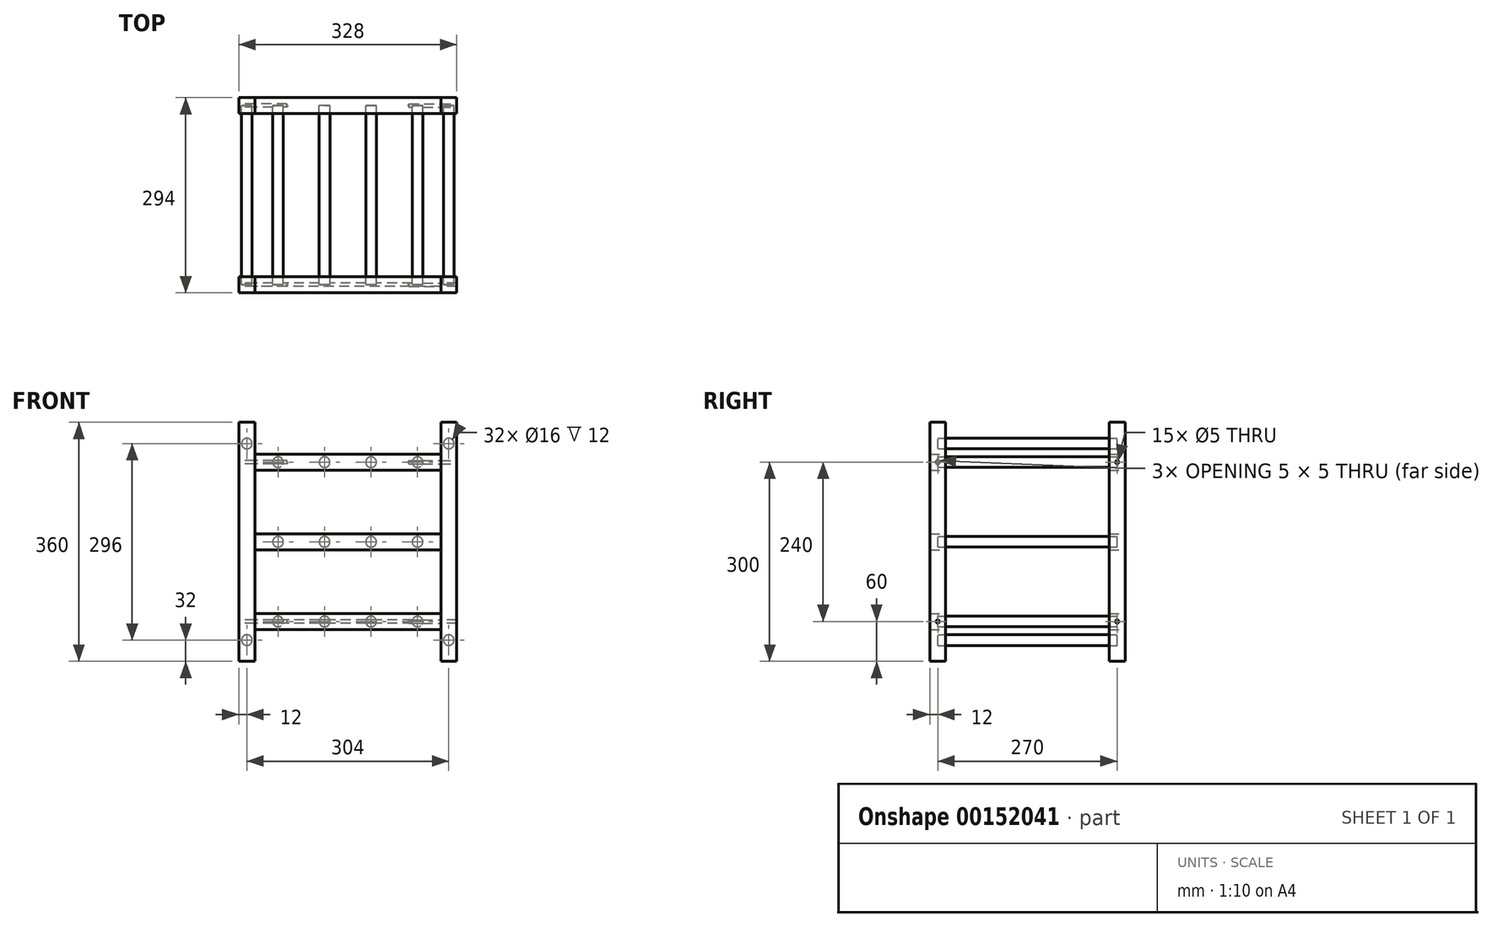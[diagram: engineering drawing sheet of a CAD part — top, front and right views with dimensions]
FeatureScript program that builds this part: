
annotation { "Feature Type Name" : "Feature", "Feature Type Description" : "" }
export const myFeature = defineFeature(function(context is Context, id is Id, definition is map)
    precondition{}
    {
        {
            assignVariable(context, id + "F0", {"name" : "Length1", "anyValue" : 270});
        }
        {
            assignVariable(context, id + "F1", {"name" : "Dia1", "anyValue" : 16 * mm});
        }
        {
            assignVariable(context, id + "F2", {"name" : "Dist1", "anyValue" : 70 * mm});
        }
        {
            assignVariable(context, id + "F3", {"name" : "Dwars1", "anyValue" : 1.5 * (getVariable(context, 'Dia1'))});
        }
        {
            assignVariable(context, id + "F4", {"name" : "Height1", "anyValue" : 120 * mm});
        }
        {
            var Q0;
            Q0=qCreatedBy(makeId("Front.planeOp"),FACE);
            var sketch = newSketch(context, id + "F5", { "sketchPlane" : qUnion([Q0])});
            skCircle(sketch, "E0", {"center": v(-105, 0) * mm, "radius": 8 * mm});
            skCircle(sketch, "E1", {"center": v(-35, 0) * mm, "radius": 8 * mm});
            skCircle(sketch, "E2", {"center": v(35, 0) * mm, "radius": 8 * mm});
            skCircle(sketch, "E3", {"center": v(105, 0) * mm, "radius": 8 * mm});
            skSolve(sketch);
        }
        {
            var Q0;
            Q0 = qSketchRegion(id + "F5", true);
            extrude(context, id + "F6", {"entities" : qUnion([Q0]), "depth" : (getVariable(context, 'Length1')) * mm});
        }
        {
            var Q0;
            Q0=qCreatedBy(makeId("Right.planeOp"),FACE);
            var sketch = newSketch(context, id + "F7", { "sketchPlane" : qUnion([Q0])});
            skLineSegment(sketch, "E4.bottom", {"start": v(-12, 12) * mm, "end": v(12, 12) * mm});
            skLineSegment(sketch, "E4.top", {"start": v(-12, -12) * mm, "end": v(12, -12) * mm});
            skLineSegment(sketch, "E4.left", {"start": v(-12, 12) * mm, "end": v(-12, -12) * mm});
            skLineSegment(sketch, "E4.right", {"start": v(12, 12) * mm, "end": v(12, -12) * mm});
            skPoint(sketch, "E5", {"position": v(12, 0) * mm});
            skPoint(sketch, "E6", {"position": v(0, 12) * mm});
            skLineSegment(sketch, "E7.bottom", {"start": v(-282, 12) * mm, "end": v(-258, 12) * mm});
            skLineSegment(sketch, "E7.top", {"start": v(-282, -12) * mm, "end": v(-258, -12) * mm});
            skLineSegment(sketch, "E7.left", {"start": v(-282, 12) * mm, "end": v(-282, -12) * mm});
            skLineSegment(sketch, "E7.right", {"start": v(-258, 12) * mm, "end": v(-258, -12) * mm});
            skPoint(sketch, "E8", {"position": v(-258, 0) * mm});
            skPoint(sketch, "E9", {"position": v(-270, 12) * mm});
            skSolve(sketch);
        }
        {
            var Q0;
            Q0 = qSketchRegion(id + "F7", true);
            extrude(context, id + "F8", {"entities" : qUnion([Q0]), "endBound" : BoundingType.SYMMETRIC, "depth" : 4 * (getVariable(context, 'Dist1'))});
        }
        {
            var Q0;
            Q0=makeQuery(id+"F6.opExtrude","SWEPT_BODY",BODY,{"disambiguationData":[OSD([sQuery(id+"F5.wireOp",EDGE,"E3")])]});
            transform(context, id + "F9", {"entities" : qUnion([Q0]), "transformType" : TransformType.COPY});
        }
        {
            var Q0;
            Q0=makeQuery(id+"F6.opExtrude","SWEPT_BODY",BODY,{"disambiguationData":[OSD([sQuery(id+"F5.wireOp",EDGE,"E0")])]});
            var Q1;
            Q1=makeQuery(id+"F6.opExtrude","SWEPT_BODY",BODY,{"disambiguationData":[OSD([sQuery(id+"F5.wireOp",EDGE,"E1")])]});
            var Q2;
            Q2=makeQuery(id+"F6.opExtrude","SWEPT_BODY",BODY,{"disambiguationData":[OSD([sQuery(id+"F5.wireOp",EDGE,"E2")])]});
            var Q3;
            Q3=makeQuery(id+"F9.opPattern","COPY",BODY,{"derivedFrom":makeQuery(id+"F6.opExtrude","SWEPT_BODY",BODY,{"disambiguationData":[OSD([sQuery(id+"F5.wireOp",EDGE,"E3")])]}),"instanceName":"1"});
            var Q4;
            Q4=makeQuery(id+"F8.opExtrude","SWEPT_BODY",BODY,{"disambiguationData":[OSD([sQuery(id+"F7.wireOp",EDGE,"E4.bottom"),sQuery(id+"F7.wireOp",EDGE,"E4.top"),sQuery(id+"F7.wireOp",EDGE,"E4.left"),sQuery(id+"F7.wireOp",EDGE,"E4.right")])]});
            var Q5;
            Q5=makeQuery(id+"F8.opExtrude","SWEPT_BODY",BODY,{"disambiguationData":[OSD([sQuery(id+"F7.wireOp",EDGE,"E7.bottom"),sQuery(id+"F7.wireOp",EDGE,"E7.top"),sQuery(id+"F7.wireOp",EDGE,"E7.left"),sQuery(id+"F7.wireOp",EDGE,"E7.right")])]});
            booleanBodies(context, id + "F10", {"operationType" : BooleanOperationType.SUBTRACTION, "tools" : qUnion([Q0, Q1, Q2, Q3]), "targets" : qUnion([Q4, Q5])});
        }
        {
            var Q0;
            Q0=makeQuery(id+"F6.opExtrude","SWEPT_BODY",BODY,{"disambiguationData":[OSD([sQuery(id+"F5.wireOp",EDGE,"E3")])]});
            transform(context, id + "F11", {"entities" : qUnion([Q0]), "transformType" : TransformType.TRANSLATION_3D, "dx" : -getVariable(context, 'Dist1'), "dy" : 0 * mm, "dz" : 0 * mm, "makeCopy" : true});
        }
        {
            var Q0;
            Q0=makeQuery(id+"F11.opPattern","COPY",BODY,{"derivedFrom":makeQuery(id+"F6.opExtrude","SWEPT_BODY",BODY,{"disambiguationData":[OSD([sQuery(id+"F5.wireOp",EDGE,"E3")])]}),"instanceName":"1"});
            var Q1;
            Q1=makeQuery(id+"F6.opExtrude","SWEPT_BODY",BODY,{"disambiguationData":[OSD([sQuery(id+"F5.wireOp",EDGE,"E3")])]});
            transform(context, id + "F12", {"entities" : qUnion([Q0, Q1]), "transformType" : TransformType.TRANSLATION_3D, "dx" : -getVariable(context, 'Dist1') * 2, "dy" : 0 * mm, "dz" : 0 * mm, "makeCopy" : true});
        }
        {
            var Q0;
            Q0=makeQuery(id+"F6.opExtrude","SWEPT_BODY",BODY,{"disambiguationData":[OSD([sQuery(id+"F5.wireOp",EDGE,"E3")])]});
            var Q1;
            Q1=makeQuery(id+"F8.opExtrude","SWEPT_BODY",BODY,{"disambiguationData":[OSD([sQuery(id+"F7.wireOp",EDGE,"E4.bottom"),sQuery(id+"F7.wireOp",EDGE,"E4.top"),sQuery(id+"F7.wireOp",EDGE,"E4.left"),sQuery(id+"F7.wireOp",EDGE,"E4.right")])]});
            var Q2;
            Q2=makeQuery(id+"F8.opExtrude","SWEPT_BODY",BODY,{"disambiguationData":[OSD([sQuery(id+"F7.wireOp",EDGE,"E7.bottom"),sQuery(id+"F7.wireOp",EDGE,"E7.top"),sQuery(id+"F7.wireOp",EDGE,"E7.left"),sQuery(id+"F7.wireOp",EDGE,"E7.right")])]});
            var Q3;
            Q3=makeQuery(id+"F11.opPattern","COPY",BODY,{"derivedFrom":makeQuery(id+"F6.opExtrude","SWEPT_BODY",BODY,{"disambiguationData":[OSD([sQuery(id+"F5.wireOp",EDGE,"E3")])]}),"instanceName":"1"});
            var Q4;
            Q4=makeQuery(id+"F12.opPattern","COPY",BODY,{"derivedFrom":makeQuery(id+"F6.opExtrude","SWEPT_BODY",BODY,{"disambiguationData":[OSD([sQuery(id+"F5.wireOp",EDGE,"E3")])]}),"instanceName":"1"});
            var Q5;
            Q5=makeQuery(id+"F12.opPattern","COPY",BODY,{"derivedFrom":makeQuery(id+"F11.opPattern","COPY",BODY,{"derivedFrom":makeQuery(id+"F6.opExtrude","SWEPT_BODY",BODY,{"disambiguationData":[OSD([sQuery(id+"F5.wireOp",EDGE,"E3")])]}),"instanceName":"1"}),"instanceName":"1"});
            transform(context, id + "F13", {"entities" : qUnion([Q0, Q1, Q2, Q3, Q4, Q5]), "transformType" : TransformType.TRANSLATION_3D, "dx" : 0 * mm, "dy" : 0 * mm, "dz" : getVariable(context, 'Height1'), "makeCopy" : true});
        }
        {
            var Q0;
            Q0=makeQuery(id+"F13.opPattern","COPY",BODY,{"derivedFrom":makeQuery(id+"F8.opExtrude","SWEPT_BODY",BODY,{"disambiguationData":[OSD([sQuery(id+"F7.wireOp",EDGE,"E7.bottom"),sQuery(id+"F7.wireOp",EDGE,"E7.top"),sQuery(id+"F7.wireOp",EDGE,"E7.left"),sQuery(id+"F7.wireOp",EDGE,"E7.right")])]}),"instanceName":"1"});
            var Q1;
            Q1=makeQuery(id+"F13.opPattern","COPY",BODY,{"derivedFrom":makeQuery(id+"F8.opExtrude","SWEPT_BODY",BODY,{"disambiguationData":[OSD([sQuery(id+"F7.wireOp",EDGE,"E4.bottom"),sQuery(id+"F7.wireOp",EDGE,"E4.top"),sQuery(id+"F7.wireOp",EDGE,"E4.left"),sQuery(id+"F7.wireOp",EDGE,"E4.right")])]}),"instanceName":"1"});
            var Q2;
            Q2=makeQuery(id+"F13.opPattern","COPY",BODY,{"derivedFrom":makeQuery(id+"F6.opExtrude","SWEPT_BODY",BODY,{"disambiguationData":[OSD([sQuery(id+"F5.wireOp",EDGE,"E3")])]}),"instanceName":"1"});
            var Q3;
            Q3=makeQuery(id+"F13.opPattern","COPY",BODY,{"derivedFrom":makeQuery(id+"F11.opPattern","COPY",BODY,{"derivedFrom":makeQuery(id+"F6.opExtrude","SWEPT_BODY",BODY,{"disambiguationData":[OSD([sQuery(id+"F5.wireOp",EDGE,"E3")])]}),"instanceName":"1"}),"instanceName":"1"});
            var Q4;
            Q4=makeQuery(id+"F13.opPattern","COPY",BODY,{"derivedFrom":makeQuery(id+"F12.opPattern","COPY",BODY,{"derivedFrom":makeQuery(id+"F6.opExtrude","SWEPT_BODY",BODY,{"disambiguationData":[OSD([sQuery(id+"F5.wireOp",EDGE,"E3")])]}),"instanceName":"1"}),"instanceName":"1"});
            var Q5;
            Q5=makeQuery(id+"F13.opPattern","COPY",BODY,{"derivedFrom":makeQuery(id+"F12.opPattern","COPY",BODY,{"derivedFrom":makeQuery(id+"F11.opPattern","COPY",BODY,{"derivedFrom":makeQuery(id+"F6.opExtrude","SWEPT_BODY",BODY,{"disambiguationData":[OSD([sQuery(id+"F5.wireOp",EDGE,"E3")])]}),"instanceName":"1"}),"instanceName":"1"}),"instanceName":"1"});
            transform(context, id + "F14", {"entities" : qUnion([Q0, Q1, Q2, Q3, Q4, Q5]), "transformType" : TransformType.TRANSLATION_3D, "dx" : 0 * mm, "dy" : 0 * mm, "dz" : getVariable(context, 'Height1'), "makeCopy" : true});
        }
        {
            var Q0;
            Q0=makeQuery(id+"F14.opPattern","COPY",FACE,{"derivedFrom":makeQuery(id+"F13.opPattern","COPY",FACE,{"derivedFrom":makeQuery(id+"F8.opExtrude","SWEPT_FACE",FACE,{"disambiguationData":[OSD([sQuery(id+"F7.wireOp",EDGE,"E7.bottom")])]}),"instanceName":"1"}),"instanceName":"1"});
            cPlane(context, id + "F15", {"entities" : qUnion([Q0]), "cplaneType" : CPlaneType.OFFSET, "offset" : getVariable(context, 'Height1') / 2 + getVariable(context, 'Dwars1') / 2, "width" : 150 * mm, "height" : 150 * mm});
        }
        {
            var Q0;
            Q0=makeQuery(id+"F14.opPattern","COPY",FACE,{"derivedFrom":makeQuery(id+"F13.opPattern","COPY",FACE,{"derivedFrom":makeQuery(id+"F8.opExtrude","CAP_FACE",FACE,{"disambiguationData":[OSD([sQuery(id+"F7.wireOp",EDGE,"E7.bottom"),sQuery(id+"F7.wireOp",EDGE,"E7.top"),sQuery(id+"F7.wireOp",EDGE,"E7.left"),sQuery(id+"F7.wireOp",EDGE,"E7.right")])],"isStart":false}),"instanceName":"1"}),"instanceName":"1"});
            cPlane(context, id + "F16", {"entities" : qUnion([Q0]), "cplaneType" : CPlaneType.OFFSET, "offset" : 0 * mm, "width" : 150 * mm, "height" : 150 * mm});
        }
        {
            var Q0;
            Q0=qCreatedBy(id+"F16.planeOp",FACE);
            var sketch = newSketch(context, id + "F17", { "sketchPlane" : qUnion([Q0])});
            skLineSegment(sketch, "E10.bottom", {"start": v(-282, 300) * mm, "end": v(-258, 300) * mm});
            skLineSegment(sketch, "E10.top", {"start": v(-282, -60) * mm, "end": v(-258, -60) * mm});
            skLineSegment(sketch, "E10.left", {"start": v(-282, 300) * mm, "end": v(-282, -60) * mm});
            skLineSegment(sketch, "E10.right", {"start": v(-258, 300) * mm, "end": v(-258, -60) * mm});
            skLineSegment(sketch, "E11", {"start": v(-282, 252) * mm, "end": v(-282, 228) * mm, "construction": true});
            skPoint(sketch, "E12", {"position": v(-282, 240) * mm});
            skLineSegment(sketch, "E13", {"start": v(-282, 12) * mm, "end": v(-282, -12) * mm, "construction": true});
            skPoint(sketch, "E14", {"position": v(-282, 0) * mm});
            skPoint(sketch, "E15", {"position": v(-282, 12) * mm});
            skPoint(sketch, "E16", {"position": v(-258, 228) * mm});
            skLineSegment(sketch, "E17", {"start": v(-258, 228) * mm, "end": v(-12, 228) * mm, "construction": true});
            skPoint(sketch, "E18", {"position": v(-135, 228) * mm});
            skLineSegment(sketch, "E19", {"start": v(-135, 228) * mm, "end": v(-135, 147.73) * mm, "construction": true});
            skLineSegment(sketch, "E20.MirrorCS", {"start": v(12, -60) * mm, "end": v(-12, -60) * mm});
            skLineSegment(sketch, "E21.MirrorCS", {"start": v(12, 300) * mm, "end": v(-12, 300) * mm});
            skLineSegment(sketch, "E22.MirrorCS", {"start": v(12, 12) * mm, "end": v(12, -12) * mm, "construction": true});
            skLineSegment(sketch, "E23.MirrorCS", {"start": v(12, 252) * mm, "end": v(12, 228) * mm, "construction": true});
            skLineSegment(sketch, "E24.MirrorCS", {"start": v(-12, 300) * mm, "end": v(-12, -60) * mm});
            skLineSegment(sketch, "E25.MirrorCS", {"start": v(12, 300) * mm, "end": v(12, -60) * mm});
            skPoint(sketch, "E26.MirrorP", {"position": v(12, 0) * mm});
            skPoint(sketch, "E27.MirrorP", {"position": v(12, 240) * mm});
            skPoint(sketch, "E28.MirrorP", {"position": v(12, 12) * mm});
            skPoint(sketch, "E29.MirrorP", {"position": v(-12, 228) * mm});
            skSolve(sketch);
        }
        {
            var Q0;
            Q0 = qSketchRegion(id + "F17", true);
            extrude(context, id + "F18", {"entities" : qUnion([Q0]), "depth" : getVariable(context, 'Dwars1')});
        }
        {
            var Q0;
            Q0=makeQuery(id+"F18.opExtrude","SWEPT_BODY",BODY,{"disambiguationData":[OSD([sQuery(id+"F17.wireOp",EDGE,"E20.MirrorCS"),sQuery(id+"F17.wireOp",EDGE,"E21.MirrorCS"),sQuery(id+"F17.wireOp",EDGE,"E24.MirrorCS"),sQuery(id+"F17.wireOp",EDGE,"E25.MirrorCS")])]});
            var Q1;
            Q1=makeQuery(id+"F18.opExtrude","SWEPT_BODY",BODY,{"disambiguationData":[OSD([sQuery(id+"F17.wireOp",EDGE,"E10.bottom"),sQuery(id+"F17.wireOp",EDGE,"E10.top"),sQuery(id+"F17.wireOp",EDGE,"E10.left"),sQuery(id+"F17.wireOp",EDGE,"E10.right")])]});
            transform(context, id + "F19", {"entities" : qUnion([Q0, Q1]), "transformType" : TransformType.TRANSLATION_3D, "dx" : -4 * getVariable(context, 'Dist1') - getVariable(context, 'Dwars1'), "dy" : 0 * mm, "dz" : 0 * mm, "makeCopy" : true});
        }
        {
            var Q0;
            Q0=makeQuery(id+"F18.opExtrude","SWEPT_FACE",FACE,{"disambiguationData":[OSD([sQuery(id+"F17.wireOp",EDGE,"E24.MirrorCS")])]});
            cPlane(context, id + "F20", {"entities" : qUnion([Q0]), "cplaneType" : CPlaneType.OFFSET, "offset" : getVariable(context, 'Dwars1') / 2, "oppositeDirection" : true, "width" : 150 * mm, "height" : 150 * mm});
        }
        {
            var Q0;
            Q0=qCreatedBy(id+"F20.planeOp",FACE);
            var sketch = newSketch(context, id + "F21", { "sketchPlane" : qUnion([Q0])});
            skCircle(sketch, "E30", {"center": v(152, 268) * mm, "radius": 8 * mm});
            skLineSegment(sketch, "E31", {"start": v(164, 268) * mm, "end": v(140, 268) * mm, "construction": true});
            skLineSegment(sketch, "E32", {"start": v(140, 300) * mm, "end": v(-140, 300) * mm, "construction": true});
            skLineSegment(sketch, "E33", {"start": v(0, 300) * mm, "end": v(0, -60) * mm, "construction": true});
            skLineSegment(sketch, "E34", {"start": v(0, 120) * mm, "end": v(-243.93, 120) * mm, "construction": true});
            skPoint(sketch, "E34.endSnap0", {"position": v(0, 120) * mm});
            skCircle(sketch, "E35.MirrorC", {"center": v(152, -28) * mm, "radius": 8 * mm});
            skCircle(sketch, "E36.MirrorC", {"center": v(-152, -28) * mm, "radius": 8 * mm});
            skCircle(sketch, "E37.MirrorC", {"center": v(-152, 268) * mm, "radius": 8 * mm});
            skSolve(sketch);
        }
        {
            var Q0;
            Q0 = qSketchRegion(id + "F21", true);
            extrude(context, id + "F22", {"entities" : qUnion([Q0]), "depth" : getVariable(context, 'Length1') * mm});
        }
        {
            var Q0;
            Q0=makeQuery(id+"F22.opExtrude","SWEPT_BODY",BODY,{"disambiguationData":[OSD([sQuery(id+"F21.wireOp",EDGE,"E30")])]});
            var Q1;
            Q1=makeQuery(id+"F22.opExtrude","SWEPT_BODY",BODY,{"disambiguationData":[OSD([sQuery(id+"F21.wireOp",EDGE,"E35.MirrorC")])]});
            var Q2;
            Q2=makeQuery(id+"F22.opExtrude","SWEPT_BODY",BODY,{"disambiguationData":[OSD([sQuery(id+"F21.wireOp",EDGE,"E36.MirrorC")])]});
            var Q3;
            Q3=makeQuery(id+"F22.opExtrude","SWEPT_BODY",BODY,{"disambiguationData":[OSD([sQuery(id+"F21.wireOp",EDGE,"E37.MirrorC")])]});
            var Q4;
            Q4=makeQuery(id+"F19.opPattern","COPY",BODY,{"derivedFrom":makeQuery(id+"F18.opExtrude","SWEPT_BODY",BODY,{"disambiguationData":[OSD([sQuery(id+"F17.wireOp",EDGE,"E10.bottom"),sQuery(id+"F17.wireOp",EDGE,"E10.top"),sQuery(id+"F17.wireOp",EDGE,"E10.left"),sQuery(id+"F17.wireOp",EDGE,"E10.right")])]}),"instanceName":"1"});
            var Q5;
            Q5=makeQuery(id+"F19.opPattern","COPY",BODY,{"derivedFrom":makeQuery(id+"F18.opExtrude","SWEPT_BODY",BODY,{"disambiguationData":[OSD([sQuery(id+"F17.wireOp",EDGE,"E20.MirrorCS"),sQuery(id+"F17.wireOp",EDGE,"E21.MirrorCS"),sQuery(id+"F17.wireOp",EDGE,"E24.MirrorCS"),sQuery(id+"F17.wireOp",EDGE,"E25.MirrorCS")])]}),"instanceName":"1"});
            var Q6;
            Q6=makeQuery(id+"F18.opExtrude","SWEPT_BODY",BODY,{"disambiguationData":[OSD([sQuery(id+"F17.wireOp",EDGE,"E20.MirrorCS"),sQuery(id+"F17.wireOp",EDGE,"E21.MirrorCS"),sQuery(id+"F17.wireOp",EDGE,"E24.MirrorCS"),sQuery(id+"F17.wireOp",EDGE,"E25.MirrorCS")])]});
            var Q7;
            Q7=makeQuery(id+"F18.opExtrude","SWEPT_BODY",BODY,{"disambiguationData":[OSD([sQuery(id+"F17.wireOp",EDGE,"E10.bottom"),sQuery(id+"F17.wireOp",EDGE,"E10.top"),sQuery(id+"F17.wireOp",EDGE,"E10.left"),sQuery(id+"F17.wireOp",EDGE,"E10.right")])]});
            booleanBodies(context, id + "F23", {"operationType" : BooleanOperationType.SUBTRACTION, "tools" : qUnion([Q0, Q1, Q2, Q3]), "targets" : qUnion([Q4, Q5, Q6, Q7]), "keepTools" : true});
        }
        {
            var Q0;
            Q0=makeQuery(id+"F19.opPattern","COPY",FACE,{"derivedFrom":makeQuery(id+"F18.opExtrude","CAP_FACE",FACE,{"disambiguationData":[OSD([sQuery(id+"F17.wireOp",EDGE,"E10.bottom"),sQuery(id+"F17.wireOp",EDGE,"E10.top"),sQuery(id+"F17.wireOp",EDGE,"E10.left"),sQuery(id+"F17.wireOp",EDGE,"E10.right")])],"isStart":true}),"instanceName":"1"});
            var sketch = newSketch(context, id + "F24", { "sketchPlane" : qUnion([Q0])});
            skLineSegment(sketch, "E38.0.0", {"start": v(258, 252) * mm, "end": v(282, 252) * mm, "construction": true});
            skLineSegment(sketch, "E38.0.1", {"start": v(282, 252) * mm, "end": v(282, 228) * mm, "construction": true});
            skLineSegment(sketch, "E38.0.2", {"start": v(282, 228) * mm, "end": v(258, 228) * mm, "construction": true});
            skLineSegment(sketch, "E38.0.3", {"start": v(258, 228) * mm, "end": v(258, 252) * mm, "construction": true});
            skLineSegment(sketch, "E39.0.0", {"start": v(258, 12) * mm, "end": v(282, 12) * mm});
            skLineSegment(sketch, "E39.0.1", {"start": v(282, 12) * mm, "end": v(282, -12) * mm});
            skLineSegment(sketch, "E39.0.2", {"start": v(282, -12) * mm, "end": v(258, -12) * mm});
            skLineSegment(sketch, "E39.0.3", {"start": v(258, -12) * mm, "end": v(258, 12) * mm});
            skLineSegment(sketch, "E40.0.0", {"start": v(-12, 12) * mm, "end": v(12, 12) * mm});
            skLineSegment(sketch, "E40.0.1", {"start": v(12, 12) * mm, "end": v(12, -12) * mm});
            skLineSegment(sketch, "E40.0.2", {"start": v(12, -12) * mm, "end": v(-12, -12) * mm});
            skLineSegment(sketch, "E40.0.3", {"start": v(-12, -12) * mm, "end": v(-12, 12) * mm});
            skLineSegment(sketch, "E41.0.0", {"start": v(-12, 252) * mm, "end": v(12, 252) * mm});
            skLineSegment(sketch, "E41.0.1", {"start": v(12, 252) * mm, "end": v(12, 228) * mm});
            skLineSegment(sketch, "E41.0.2", {"start": v(12, 228) * mm, "end": v(-12, 228) * mm});
            skLineSegment(sketch, "E41.0.3", {"start": v(-12, 228) * mm, "end": v(-12, 252) * mm});
            skLineSegment(sketch, "E42", {"start": v(282, 252) * mm, "end": v(258, 228) * mm, "construction": true});
            skLineSegment(sketch, "E43", {"start": v(258, 252) * mm, "end": v(282, 228) * mm, "construction": true});
            skPoint(sketch, "E44", {"position": v(270, 240) * mm});
            skPoint(sketch, "E45", {"position": v(0, 240) * mm});
            skPoint(sketch, "E45.positionSnap0", {"position": v(12, 240) * mm});
            skPoint(sketch, "E45.positionSnap1", {"position": v(0, 252) * mm});
            skPoint(sketch, "E46", {"position": v(0, 0) * mm});
            skPoint(sketch, "E47", {"position": v(270, 0) * mm});
            skPoint(sketch, "E47.positionSnap0", {"position": v(258, 0) * mm});
            skPoint(sketch, "E47.positionSnap1", {"position": v(270, 12) * mm});
            skSolve(sketch);
        }
        {
            var Q0;
            Q0=sQuery(id+"F24.wireOp",VERTEX,"E47");
            var Q1;
            Q1=sQuery(id+"F24.wireOp",VERTEX,"E44");
            var Q2;
            Q2=sQuery(id+"F24.wireOp",VERTEX,"E45");
            var Q3;
            Q3=sQuery(id+"F24.wireOp",VERTEX,"E46");
            var Q4;
            Q4=makeQuery(id+"F19.opPattern","COPY",BODY,{"derivedFrom":makeQuery(id+"F18.opExtrude","SWEPT_BODY",BODY,{"disambiguationData":[OSD([sQuery(id+"F17.wireOp",EDGE,"E10.bottom"),sQuery(id+"F17.wireOp",EDGE,"E10.top"),sQuery(id+"F17.wireOp",EDGE,"E10.left"),sQuery(id+"F17.wireOp",EDGE,"E10.right")])]}),"instanceName":"1"});
            var Q5;
            Q5=makeQuery(id+"F19.opPattern","COPY",BODY,{"derivedFrom":makeQuery(id+"F18.opExtrude","SWEPT_BODY",BODY,{"disambiguationData":[OSD([sQuery(id+"F17.wireOp",EDGE,"E20.MirrorCS"),sQuery(id+"F17.wireOp",EDGE,"E21.MirrorCS"),sQuery(id+"F17.wireOp",EDGE,"E24.MirrorCS"),sQuery(id+"F17.wireOp",EDGE,"E25.MirrorCS")])]}),"instanceName":"1"});
            var Q6;
            Q6=makeQuery(id+"F14.opPattern","COPY",BODY,{"derivedFrom":makeQuery(id+"F13.opPattern","COPY",BODY,{"derivedFrom":makeQuery(id+"F8.opExtrude","SWEPT_BODY",BODY,{"disambiguationData":[OSD([sQuery(id+"F7.wireOp",EDGE,"E4.bottom"),sQuery(id+"F7.wireOp",EDGE,"E4.top"),sQuery(id+"F7.wireOp",EDGE,"E4.left"),sQuery(id+"F7.wireOp",EDGE,"E4.right")])]}),"instanceName":"1"}),"instanceName":"1"});
            var Q7;
            Q7=makeQuery(id+"F8.opExtrude","SWEPT_BODY",BODY,{"disambiguationData":[OSD([sQuery(id+"F7.wireOp",EDGE,"E4.bottom"),sQuery(id+"F7.wireOp",EDGE,"E4.top"),sQuery(id+"F7.wireOp",EDGE,"E4.left"),sQuery(id+"F7.wireOp",EDGE,"E4.right")])]});
            var Q8;
            Q8=makeQuery(id+"F8.opExtrude","SWEPT_BODY",BODY,{"disambiguationData":[OSD([sQuery(id+"F7.wireOp",EDGE,"E7.bottom"),sQuery(id+"F7.wireOp",EDGE,"E7.top"),sQuery(id+"F7.wireOp",EDGE,"E7.left"),sQuery(id+"F7.wireOp",EDGE,"E7.right")])]});
            var Q9;
            Q9=makeQuery(id+"F14.opPattern","COPY",BODY,{"derivedFrom":makeQuery(id+"F13.opPattern","COPY",BODY,{"derivedFrom":makeQuery(id+"F8.opExtrude","SWEPT_BODY",BODY,{"disambiguationData":[OSD([sQuery(id+"F7.wireOp",EDGE,"E7.bottom"),sQuery(id+"F7.wireOp",EDGE,"E7.top"),sQuery(id+"F7.wireOp",EDGE,"E7.left"),sQuery(id+"F7.wireOp",EDGE,"E7.right")])]}),"instanceName":"1"}),"instanceName":"1"});
            hole(context, id + "F25", {"style" : HoleStyle.SIMPLE, "endStyle" : HoleEndStyle.BLIND_IN_LAST, "holeDiameter" : 5 * mm, "tapDrillDiameter" : 5 * mm, "holeDepth" : getVariable(context, 'Dwars1') * 2, "startFromSketch" : true, "locations" : qUnion([Q0, Q1, Q2, Q3]), "scope" : qUnion([Q4, Q5, Q6, Q7, Q8, Q9])});
        }
        {
            var Q0;
            Q0=makeQuery(id+"F18.opExtrude","CAP_FACE",FACE,{"disambiguationData":[OSD([sQuery(id+"F17.wireOp",EDGE,"E20.MirrorCS"),sQuery(id+"F17.wireOp",EDGE,"E21.MirrorCS"),sQuery(id+"F17.wireOp",EDGE,"E24.MirrorCS"),sQuery(id+"F17.wireOp",EDGE,"E25.MirrorCS")])],"isStart":false});
            var sketch = newSketch(context, id + "F26", { "sketchPlane" : qUnion([Q0])});
            skLineSegment(sketch, "E48.0.0", {"start": v(-258, 252) * mm, "end": v(-282, 252) * mm, "construction": true});
            skLineSegment(sketch, "E48.0.1", {"start": v(-282, 252) * mm, "end": v(-282, 228) * mm, "construction": true});
            skLineSegment(sketch, "E48.0.2", {"start": v(-282, 228) * mm, "end": v(-258, 228) * mm, "construction": true});
            skLineSegment(sketch, "E48.0.3", {"start": v(-258, 228) * mm, "end": v(-258, 252) * mm, "construction": true});
            skLineSegment(sketch, "E49.0.0", {"start": v(-258, 12) * mm, "end": v(-282, 12) * mm});
            skLineSegment(sketch, "E49.0.1", {"start": v(-282, 12) * mm, "end": v(-282, -12) * mm});
            skLineSegment(sketch, "E49.0.2", {"start": v(-282, -12) * mm, "end": v(-258, -12) * mm});
            skLineSegment(sketch, "E49.0.3", {"start": v(-258, -12) * mm, "end": v(-258, 12) * mm});
            skLineSegment(sketch, "E50.0.0", {"start": v(12, 252) * mm, "end": v(-12, 252) * mm});
            skLineSegment(sketch, "E50.0.1", {"start": v(-12, 252) * mm, "end": v(-12, 228) * mm});
            skLineSegment(sketch, "E50.0.2", {"start": v(-12, 228) * mm, "end": v(12, 228) * mm});
            skLineSegment(sketch, "E50.0.3", {"start": v(12, 228) * mm, "end": v(12, 252) * mm});
            skLineSegment(sketch, "E51.0.0", {"start": v(12, 12) * mm, "end": v(-12, 12) * mm});
            skLineSegment(sketch, "E51.0.1", {"start": v(-12, 12) * mm, "end": v(-12, -12) * mm});
            skLineSegment(sketch, "E51.0.2", {"start": v(-12, -12) * mm, "end": v(12, -12) * mm});
            skLineSegment(sketch, "E51.0.3", {"start": v(12, -12) * mm, "end": v(12, 12) * mm});
            skLineSegment(sketch, "E52", {"start": v(-282, 252) * mm, "end": v(-258, 228) * mm, "construction": true});
            skPoint(sketch, "E53", {"position": v(-270, 240) * mm});
            skPoint(sketch, "E54", {"position": v(0, 240) * mm});
            skPoint(sketch, "E54.positionSnap0", {"position": v(-12, 240) * mm});
            skPoint(sketch, "E54.positionSnap1", {"position": v(0, 252) * mm});
            skPoint(sketch, "E55", {"position": v(0, 0) * mm});
            skPoint(sketch, "E56", {"position": v(-270, 0) * mm});
            skPoint(sketch, "E56.positionSnap0", {"position": v(-270, 12) * mm});
            skPoint(sketch, "E56.positionSnap1", {"position": v(-258, 0) * mm});
            skSolve(sketch);
        }
        {
            var Q0;
            Q0=sQuery(id+"F24.wireOp",VERTEX,"E47");
            var Q1;
            Q1=sQuery(id+"F26.wireOp",VERTEX,"E53");
            var Q2;
            Q2=sQuery(id+"F26.wireOp",VERTEX,"E54");
            var Q3;
            Q3=sQuery(id+"F26.wireOp",VERTEX,"E55");
            var Q4;
            Q4=makeQuery(id+"F18.opExtrude","SWEPT_BODY",BODY,{"disambiguationData":[OSD([sQuery(id+"F17.wireOp",EDGE,"E10.bottom"),sQuery(id+"F17.wireOp",EDGE,"E10.top"),sQuery(id+"F17.wireOp",EDGE,"E10.left"),sQuery(id+"F17.wireOp",EDGE,"E10.right")])]});
            var Q5;
            Q5=makeQuery(id+"F18.opExtrude","SWEPT_BODY",BODY,{"disambiguationData":[OSD([sQuery(id+"F17.wireOp",EDGE,"E20.MirrorCS"),sQuery(id+"F17.wireOp",EDGE,"E21.MirrorCS"),sQuery(id+"F17.wireOp",EDGE,"E24.MirrorCS"),sQuery(id+"F17.wireOp",EDGE,"E25.MirrorCS")])]});
            var Q6;
            Q6=makeQuery(id+"F14.opPattern","COPY",BODY,{"derivedFrom":makeQuery(id+"F13.opPattern","COPY",BODY,{"derivedFrom":makeQuery(id+"F8.opExtrude","SWEPT_BODY",BODY,{"disambiguationData":[OSD([sQuery(id+"F7.wireOp",EDGE,"E4.bottom"),sQuery(id+"F7.wireOp",EDGE,"E4.top"),sQuery(id+"F7.wireOp",EDGE,"E4.left"),sQuery(id+"F7.wireOp",EDGE,"E4.right")])]}),"instanceName":"1"}),"instanceName":"1"});
            var Q7;
            Q7=makeQuery(id+"F14.opPattern","COPY",BODY,{"derivedFrom":makeQuery(id+"F13.opPattern","COPY",BODY,{"derivedFrom":makeQuery(id+"F8.opExtrude","SWEPT_BODY",BODY,{"disambiguationData":[OSD([sQuery(id+"F7.wireOp",EDGE,"E7.bottom"),sQuery(id+"F7.wireOp",EDGE,"E7.top"),sQuery(id+"F7.wireOp",EDGE,"E7.left"),sQuery(id+"F7.wireOp",EDGE,"E7.right")])]}),"instanceName":"1"}),"instanceName":"1"});
            var Q8;
            Q8=makeQuery(id+"F8.opExtrude","SWEPT_BODY",BODY,{"disambiguationData":[OSD([sQuery(id+"F7.wireOp",EDGE,"E7.bottom"),sQuery(id+"F7.wireOp",EDGE,"E7.top"),sQuery(id+"F7.wireOp",EDGE,"E7.left"),sQuery(id+"F7.wireOp",EDGE,"E7.right")])]});
            var Q9;
            Q9=makeQuery(id+"F8.opExtrude","SWEPT_BODY",BODY,{"disambiguationData":[OSD([sQuery(id+"F7.wireOp",EDGE,"E4.bottom"),sQuery(id+"F7.wireOp",EDGE,"E4.top"),sQuery(id+"F7.wireOp",EDGE,"E4.left"),sQuery(id+"F7.wireOp",EDGE,"E4.right")])]});
            hole(context, id + "F27", {"style" : HoleStyle.SIMPLE, "endStyle" : HoleEndStyle.BLIND_IN_LAST, "holeDiameter" : 5 * mm, "tapDrillDiameter" : 5 * mm, "holeDepth" : getVariable(context, 'Dwars1') * 2, "startFromSketch" : true, "locations" : qUnion([Q0, Q1, Q2, Q3]), "scope" : qUnion([Q4, Q5, Q6, Q7, Q8, Q9])});
        }
    });
